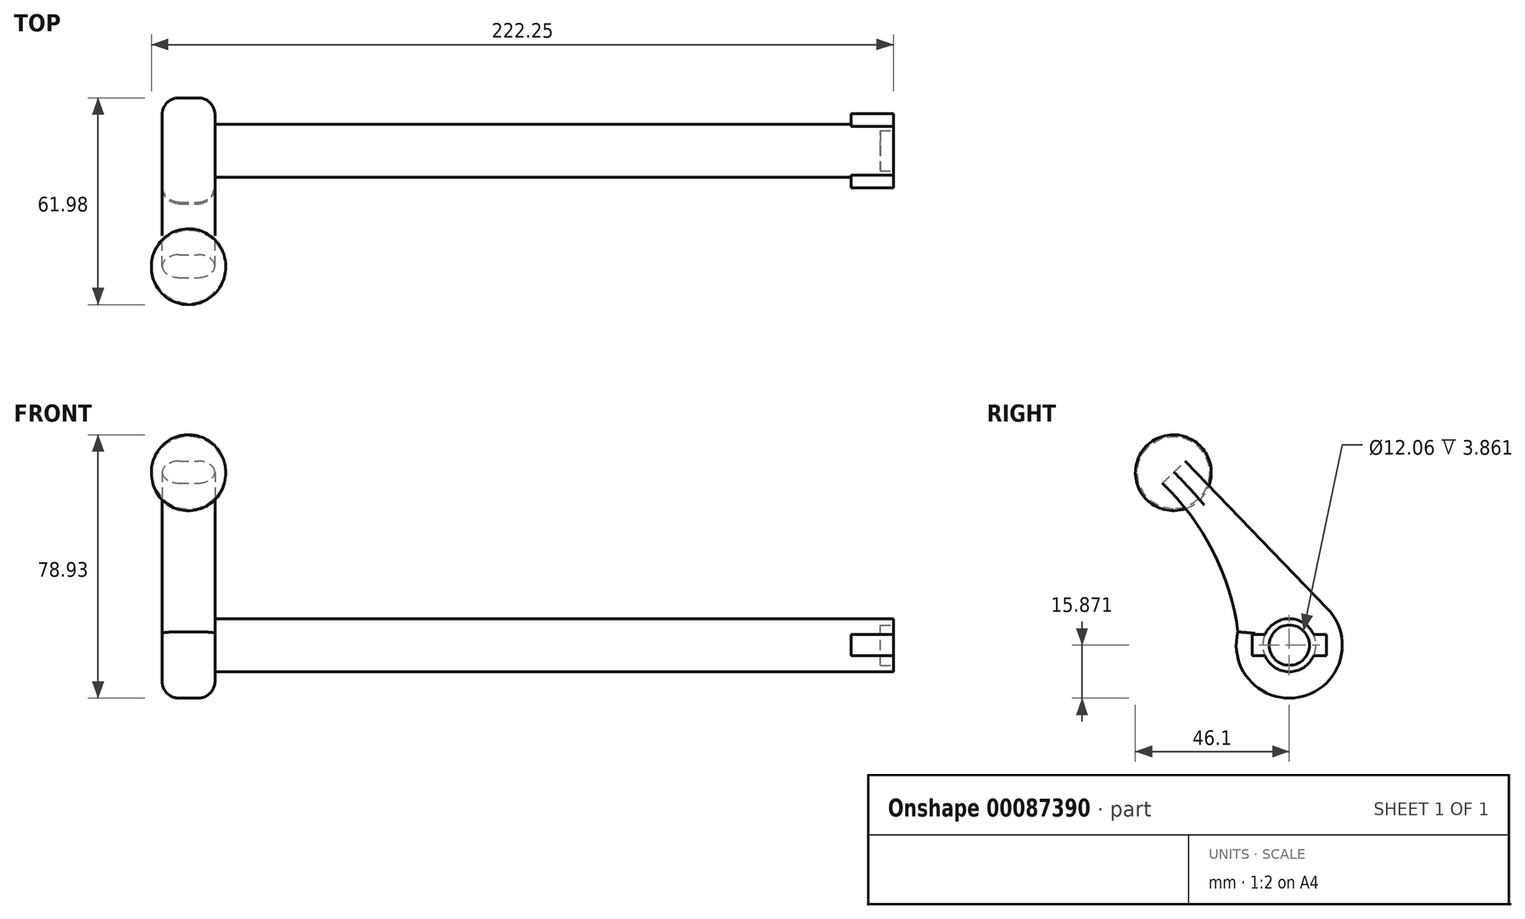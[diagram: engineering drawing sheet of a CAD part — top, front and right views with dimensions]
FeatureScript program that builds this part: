
annotation { "Feature Type Name" : "Feature", "Feature Type Description" : "" }
export const myFeature = defineFeature(function(context is Context, id is Id, definition is map)
    precondition{}
    {
        {
            var Q0;
            Q0=qCreatedBy(makeId("Front.planeOp"),FACE);
            var sketch = newSketch(context, id + "F0", { "sketchPlane" : qUnion([Q0])});
            skLineSegment(sketch, "E0.bottom", {"start": v(101.6, -3.97) * mm, "end": v(-101.6, -3.97) * mm});
            skLineSegment(sketch, "E0.top", {"start": v(101.6, 3.97) * mm, "end": v(-101.6, 3.97) * mm});
            skLineSegment(sketch, "E0.left", {"start": v(101.6, -3.97) * mm, "end": v(101.6, 3.97) * mm});
            skLineSegment(sketch, "E0.right", {"start": v(-101.6, -3.97) * mm, "end": v(-101.6, 3.97) * mm});
            skPoint(sketch, "E0.middle", {"position": v(0, 0) * mm});
            skSolve(sketch);
        }
        {
            var Q0;
            Q0 = qSketchRegion(id + "F0", true);
            var Q1;
            Q1=sQuery(id+"F0.wireOp",EDGE,"E0.bottom");
            revolve(context, id + "F1", {"entities" : qUnion([Q0]), "axis" : qUnion([Q1]), "revolveType" : RevolveType.FULL});
        }
        {
            var Q0;
            Q0=makeQuery(id+"F1.opRevolve","SWEPT_FACE",FACE,{"disambiguationData":[OSD([sQuery(id+"F0.wireOp",EDGE,"E0.left")])]});
            var sketch = newSketch(context, id + "F2", { "sketchPlane" : qUnion([Q0])});
            skLineSegment(sketch, "E1.bottom", {"start": v(11.11, -7.14) * mm, "end": v(-11.11, -7.14) * mm});
            skLineSegment(sketch, "E1.top", {"start": v(11.11, -0.8) * mm, "end": v(-11.11, -0.8) * mm});
            skLineSegment(sketch, "E1.left", {"start": v(11.11, -7.14) * mm, "end": v(11.11, -0.8) * mm});
            skLineSegment(sketch, "E1.right", {"start": v(-11.11, -7.14) * mm, "end": v(-11.11, -0.8) * mm});
            skPoint(sketch, "E1.middle", {"position": v(0, -3.97) * mm});
            skSolve(sketch);
        }
        {
            var Q0;
            Q0 = qSketchRegion(id + "F2", true);
            extrude(context, id + "F3", {"entities" : qUnion([Q0]), "operationType" : NewBodyOperationType.ADD, "oppositeDirection" : true, "depth" : 12.7 * mm});
        }
        {
            var Q0;
            Q0=makeQuery(id+"F3.boolean.opBoolean","MERGE",FACE,{"derivedFrom":[makeQuery(id+"F1.opRevolve","SWEPT_FACE",FACE,{"disambiguationData":[OSD([sQuery(id+"F0.wireOp",EDGE,"E0.left")])]}),makeQuery(id+"F3.opExtrude","CAP_FACE",FACE,{"disambiguationData":[OSD([sQuery(id+"F2.wireOp",EDGE,"E1.bottom"),sQuery(id+"F2.wireOp",EDGE,"E1.top"),sQuery(id+"F2.wireOp",EDGE,"E1.left"),sQuery(id+"F2.wireOp",EDGE,"E1.right")])],"isStart":true})]});
            var sketch = newSketch(context, id + "F4", { "sketchPlane" : qUnion([Q0])});
            skCircle(sketch, "E2", {"center": v(0, -3.97) * mm, "radius": 6.03 * mm});
            skSolve(sketch);
        }
        {
            var Q0;
            Q0 = qSketchRegion(id + "F4", true);
            extrude(context, id + "F5", {"entities" : qUnion([Q0]), "operationType" : NewBodyOperationType.REMOVE, "oppositeDirection" : true, "depth" : 3.86 * mm});
        }
        {
            var Q0;
            Q0=makeQuery(id+"F1.opRevolve","SWEPT_FACE",FACE,{"disambiguationData":[OSD([sQuery(id+"F0.wireOp",EDGE,"E0.right")])]});
            var sketch = newSketch(context, id + "F6", { "sketchPlane" : qUnion([Q0])});
            skArc(sketch, "E3", {"start": v(-11.43, 7.05) * mm, "mid": v(-4.04, -19.32) * mm, "end": v(15.37, 0) * mm});
            skLineSegment(sketch, "E4", {"start": v(-11.43, 7.05) * mm, "end": v(31.12, 51.2) * mm});
            skLineSegment(sketch, "E5", {"start": v(31.12, 51.2) * mm, "end": v(37.98, 44.6) * mm});
            skArc(sketch, "E6", {"start": v(37.98, 44.6) * mm, "mid": v(22.9, 24.21) * mm, "end": v(15.37, 0) * mm});
            skPoint(sketch, "E7.start.orphan", {"position": v(26.67, 22.3) * mm});
            skSolve(sketch);
        }
        {
            var Q0;
            Q0 = qSketchRegion(id + "F6", true);
            extrude(context, id + "F7", {"entities" : qUnion([Q0]), "operationType" : NewBodyOperationType.ADD, "depth" : 15.88 * mm});
        }
        {
            var Q0;
            Q0=makeQuery(id+"F7.opExtrude","CAP_EDGE",EDGE,{"disambiguationData":[OSD([sQuery(id+"F6.wireOp",EDGE,"E4")])],"isStart":false});
            var Q1;
            Q1=makeQuery(id+"F7.opExtrude","CAP_EDGE",EDGE,{"disambiguationData":[OSD([sQuery(id+"F6.wireOp",EDGE,"E3")])],"isStart":false});
            var Q2;
            Q2=makeQuery(id+"F7.opExtrude","CAP_EDGE",EDGE,{"disambiguationData":[OSD([sQuery(id+"F6.wireOp",EDGE,"E6")])],"isStart":false});
            var Q3;
            Q3=makeQuery(id+"F7.opExtrude","CAP_EDGE",EDGE,{"disambiguationData":[OSD([sQuery(id+"F6.wireOp",EDGE,"E4")])],"isStart":true});
            var Q4;
            Q4=makeQuery(id+"F7.opExtrude","CAP_EDGE",EDGE,{"disambiguationData":[OSD([sQuery(id+"F6.wireOp",EDGE,"E6")])],"isStart":true});
            fillet(context, id + "F8", {"entities" : qUnion([Q0, Q1, Q2, Q3, Q4]), "radius" : 5.08 * mm, "tangentPropagation" : true, "allowEdgeOverflow" : false});
        }
        {
            var Q0;
            Q0=makeQuery(id+"F7.opExtrude","SWEPT_FACE",FACE,{"disambiguationData":[OSD([sQuery(id+"F6.wireOp",EDGE,"E5")])]});
            var sketch = newSketch(context, id + "F9", { "sketchPlane" : qUnion([Q0])});
            skLineSegment(sketch, "E8", {"start": v(-101.61, 8.36) * mm, "end": v(-117.46, 8.36) * mm});
            skArc(sketch, "E9", {"start": v(-98.43, 8.1) * mm, "mid": v(-109.54, 19.47) * mm, "end": v(-120.65, 8.1) * mm});
            skLineSegment(sketch, "E10", {"start": v(-120.65, 8.1) * mm, "end": v(-98.43, 8.1) * mm});
            skSolve(sketch);
        }
        {
            var Q0;
            Q0 = qSketchRegion(id + "F9", true);
            var Q1;
            Q1=sQuery(id+"F9.wireOp",EDGE,"E10");
            revolve(context, id + "F10", {"entities" : qUnion([Q0]), "axis" : qUnion([Q1]), "revolveType" : RevolveType.FULL});
        }
    });
